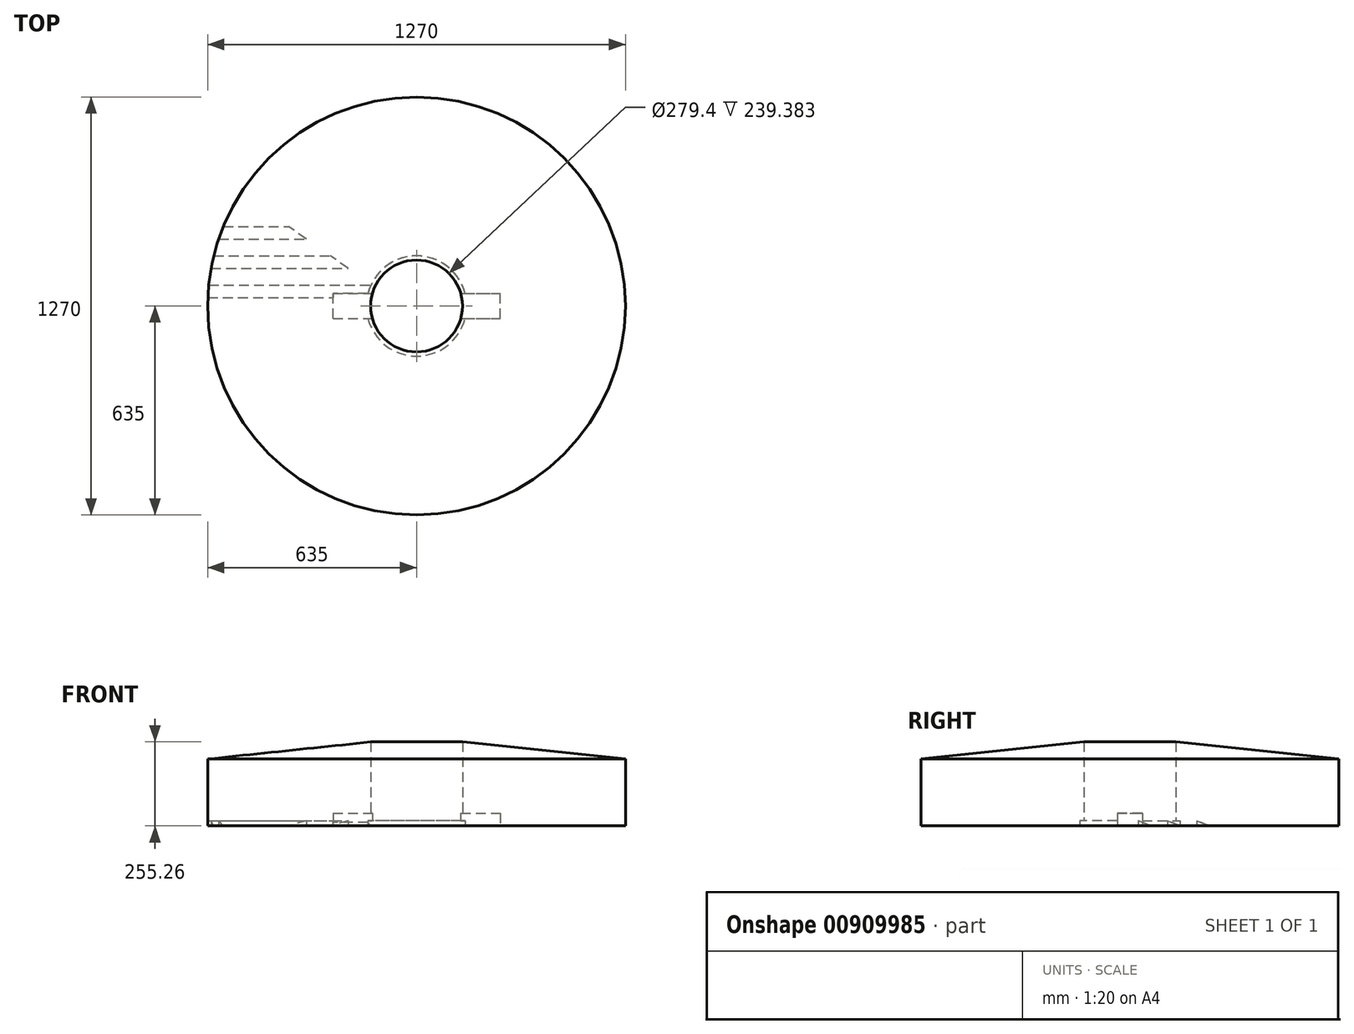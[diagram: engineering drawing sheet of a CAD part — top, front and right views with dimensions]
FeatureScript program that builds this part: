
annotation { "Feature Type Name" : "Feature", "Feature Type Description" : "" }
export const myFeature = defineFeature(function(context is Context, id is Id, definition is map)
    precondition{}
    {
        {
            var Q0;
            Q0=qCreatedBy(makeId("Front.planeOp"),FACE);
            var sketch = newSketch(context, id + "F0", { "sketchPlane" : qUnion([Q0])});
            skLineSegment(sketch, "E0", {"start": v(139.7, 0) * mm, "end": v(635, 0) * mm});
            skLineSegment(sketch, "E1", {"start": v(635, 0) * mm, "end": v(635, 203.2) * mm});
            skLineSegment(sketch, "E2", {"start": v(635, 203.2) * mm, "end": v(139.7, 255.26) * mm});
            skLineSegment(sketch, "E3", {"start": v(139.7, 255.26) * mm, "end": v(139.7, 0) * mm});
            skLineSegment(sketch, "E4", {"start": v(0, 0) * mm, "end": v(0, 255.26) * mm, "construction": true});
            skSolve(sketch);
        }
        {
            var Q0;
            Q0=makeQuery(id+"F0.imprint","IMPRINT",FACE,{"disambiguationData":[TD([[makeQuery(id+"F0.imprint","IMPRINT",EDGE,{"derivedFrom":sQuery(id+"F0.wireOp",EDGE,"E0")}),1.0]])]});
            var Q1;
            Q1=sQuery(id+"F0.wireOp",EDGE,"E4");
            revolve(context, id + "F1", {"surfaceOperationType" : NewSurfaceOperationType.NEW, "entities" : qUnion([Q0]), "axis" : qUnion([Q1]), "revolveType" : RevolveType.FULL});
        }
        {
            var Q0;
            Q0=makeQuery(id+"F1.opRevolve","SWEPT_FACE",FACE,{"disambiguationData":[OSD([sQuery(id+"F0.wireOp",EDGE,"E0")])]});
            var sketch = newSketch(context, id + "F2", { "sketchPlane" : qUnion([Q0])});
            skLineSegment(sketch, "E5.bottom", {"start": v(-634.5, -25.4) * mm, "end": v(-37.18, -25.4) * mm});
            skLineSegment(sketch, "E5.top", {"start": v(-634.5, -63.5) * mm, "end": v(-37.18, -63.5) * mm});
            skLineSegment(sketch, "E5.left", {"start": v(-634.5, -25.4) * mm, "end": v(-634.5, -63.5) * mm});
            skLineSegment(sketch, "E5.right", {"start": v(-37.18, -25.4) * mm, "end": v(-37.18, -63.5) * mm});
            skLineSegment(sketch, "E6.bottom", {"start": v(-624.63, -114.3) * mm, "end": v(-207.52, -114.3) * mm});
            skLineSegment(sketch, "E6.top", {"start": v(-624.63, -152.4) * mm, "end": v(-261.93, -152.4) * mm});
            skLineSegment(sketch, "E6.left", {"start": v(-624.63, -114.3) * mm, "end": v(-624.63, -152.4) * mm});
            skLineSegment(sketch, "E7.bottom", {"start": v(-601.61, -203.2) * mm, "end": v(-334.48, -203.2) * mm});
            skLineSegment(sketch, "E7.top", {"start": v(-601.61, -241.3) * mm, "end": v(-388.9, -241.3) * mm});
            skLineSegment(sketch, "E7.left", {"start": v(-601.61, -203.2) * mm, "end": v(-601.61, -241.3) * mm});
            skLineSegment(sketch, "E8", {"start": v(-524.9, -25.4) * mm, "end": v(-524.9, -114.3) * mm, "construction": true});
            skLineSegment(sketch, "E9", {"start": v(-524.9, -114.3) * mm, "end": v(-524.9, -203.2) * mm, "construction": true});
            skLineSegment(sketch, "E10", {"start": v(-207.52, -114.3) * mm, "end": v(-261.93, -152.4) * mm});
            skLineSegment(sketch, "E11.trimOffspring", {"start": v(-334.48, -203.2) * mm, "end": v(-388.9, -241.3) * mm});
            skCircle(sketch, "E12", {"center": v(0, 0) * mm, "radius": 152.4 * mm});
            skSolve(sketch);
        }
        {
            var Q0;
            {var subQ1=sQuery(id+"F0.wireOp",EDGE,"E0");var subQ2=makeQuery(id+"F1.opRevolve","SWEPT_EDGE",EDGE,{"disambiguationData":[OSD([subQ1,sQuery(id+"F0.wireOp",EDGE,"E1")])]});var subQ6=sQuery(id+"F2.wireOp",EDGE,"E5.top");var subQ7=makeQuery(id+"F2.imprint","INTERSECT",VERTEX,{"derivedFrom":[subQ2,subQ6]});Q0=makeQuery(id+"F2.imprint","IMPRINT",FACE,{"disambiguationData":[TD([[makeQuery(id+"F2.imprint","IMPRINT",EDGE,{"disambiguationData":[TD([[subQ7,-1.0]])],"derivedFrom":subQ6}),1.0]])]});}
            var Q1;
            {var subQ0=sQuery(id+"F2.wireOp",EDGE,"E6.bottom");Q1=makeQuery(id+"F2.imprint","IMPRINT",FACE,{"disambiguationData":[TD([[makeQuery(id+"F2.imprint","IMPRINT",EDGE,{"derivedFrom":subQ0}),-1.0]])]});}
            var Q2;
            {var subQ0=sQuery(id+"F2.wireOp",EDGE,"E7.bottom");Q2=makeQuery(id+"F2.imprint","IMPRINT",FACE,{"disambiguationData":[TD([[makeQuery(id+"F2.imprint","IMPRINT",EDGE,{"derivedFrom":subQ0}),-1.0]])]});}
            extrude(context, id + "F3", {"entities" : qUnion([Q0, Q1, Q2]), "operationType" : NewBodyOperationType.REMOVE, "oppositeDirection" : true, "depth" : 15.88 * mm, "offsetDistance" : 25 * mm});
        }
        {
            var Q0;
            {var subQ0=sQuery(id+"F2.wireOp",EDGE,"E12");var subQ1=sQuery(id+"F2.wireOp",EDGE,"E5.bottom");var subQ2=makeQuery(id+"F2.imprint","INTERSECT",VERTEX,{"derivedFrom":[subQ1,subQ0]});Q0=makeQuery(id+"F2.imprint","IMPRINT",FACE,{"disambiguationData":[TD([[makeQuery(id+"F2.imprint","IMPRINT",EDGE,{"disambiguationData":[TD([[subQ2,1.0]])],"derivedFrom":subQ0}),1.0]])]});}
            var Q1;
            {var subQ0=sQuery(id+"F2.wireOp",EDGE,"E5.right");Q1=makeQuery(id+"F2.imprint","IMPRINT",FACE,{"disambiguationData":[TD([[makeQuery(id+"F2.imprint","IMPRINT",EDGE,{"derivedFrom":subQ0}),-1.0]])]});}
            var Q2;
            {var subQ0=sQuery(id+"F2.wireOp",EDGE,"E12");var subQ1=sQuery(id+"F2.wireOp",EDGE,"E5.bottom");var subQ2=makeQuery(id+"F2.imprint","INTERSECT",VERTEX,{"derivedFrom":[subQ1,subQ0]});Q2=makeQuery(id+"F2.imprint","IMPRINT",FACE,{"disambiguationData":[TD([[makeQuery(id+"F2.imprint","IMPRINT",EDGE,{"disambiguationData":[TD([[subQ2,-1.0]])],"derivedFrom":subQ0}),1.0]])]});}
            extrude(context, id + "F4", {"entities" : qUnion([Q0, Q1, Q2]), "operationType" : NewBodyOperationType.REMOVE, "oppositeDirection" : true, "depth" : 15.88 * mm, "offsetDistance" : 25 * mm});
        }
        {
            var Q0;
            Q0=makeQuery(id+"F3.boolean.opBoolean","COPY",EDGE,{"derivedFrom":makeQuery(id+"F3.opExtrude","CAP_EDGE",EDGE,{"disambiguationData":[OSD([sQuery(id+"F2.wireOp",EDGE,"E5.top")])],"isStart":false})});
            var Q1;
            Q1=makeQuery(id+"F3.boolean.opBoolean","COPY",EDGE,{"derivedFrom":makeQuery(id+"F3.opExtrude","CAP_EDGE",EDGE,{"disambiguationData":[OSD([sQuery(id+"F2.wireOp",EDGE,"E6.top")])],"isStart":false})});
            var Q2;
            Q2=makeQuery(id+"F3.boolean.opBoolean","COPY",EDGE,{"derivedFrom":makeQuery(id+"F3.opExtrude","CAP_EDGE",EDGE,{"disambiguationData":[OSD([sQuery(id+"F2.wireOp",EDGE,"E7.top")])],"isStart":false})});
            chamfer(context, id + "F5", {"entities" : qUnion([Q0, Q1, Q2]), "chamferType" : ChamferType.TWO_OFFSETS, "width1" : 38.1 * mm, "oppositeDirection" : false, "width2" : 15.88 * mm, "tangentPropagation" : true});
        }
        {
            var Q0;
            {var subQ13=sQuery(id+"F2.wireOp",EDGE,"E6.bottom");Q0=makeQuery(id+"F2.imprint","IMPRINT",FACE,{"disambiguationData":[TD([[makeQuery(id+"F2.imprint","IMPRINT",EDGE,{"derivedFrom":subQ13}),1.0]])]});}
            var sketch = newSketch(context, id + "F6", { "sketchPlane" : qUnion([Q0])});
            skLineSegment(sketch, "E13.bottom", {"start": v(-254, 38.1) * mm, "end": v(254, 38.1) * mm});
            skLineSegment(sketch, "E13.top", {"start": v(-254, -38.1) * mm, "end": v(254, -38.1) * mm});
            skLineSegment(sketch, "E13.left", {"start": v(-254, 38.1) * mm, "end": v(-254, -38.1) * mm});
            skLineSegment(sketch, "E13.right", {"start": v(254, 38.1) * mm, "end": v(254, -38.1) * mm});
            skLineSegment(sketch, "E14", {"start": v(-254, 0) * mm, "end": v(254, 0) * mm, "construction": true});
            skLineSegment(sketch, "E15", {"start": v(0, 38.1) * mm, "end": v(0, -38.1) * mm, "construction": true});
            skSolve(sketch);
        }
        {
            var Q0;
            {var subQ0=sQuery(id+"F6.wireOp",EDGE,"E13.bottom");var subQ1=sQuery(id+"F2.wireOp",EDGE,"E12");var subQ2=makeQuery(id+"F2.imprint","IMPRINT",EDGE,{"disambiguationData":[TD([[makeQuery(id+"F2.imprint","INTERSECT",VERTEX,{"derivedFrom":[sQuery(id+"F2.wireOp",EDGE,"E5.bottom"),subQ1]}),1.0]])],"derivedFrom":subQ1});var subQ3=makeQuery(id+"F6.imprint","INTERSECT",VERTEX,{"disambiguationData":[OD(0.0)],"derivedFrom":[subQ2,subQ0]});Q0=makeQuery(id+"F6.imprint","IMPRINT",FACE,{"disambiguationData":[TD([[makeQuery(id+"F6.imprint","IMPRINT",EDGE,{"disambiguationData":[TD([[subQ3,-1.0]])],"derivedFrom":subQ0}),-1.0]])]});}
            var Q1;
            {var subQ0=sQuery(id+"F6.wireOp",EDGE,"E13.left");Q1=makeQuery(id+"F6.imprint","IMPRINT",FACE,{"disambiguationData":[TD([[makeQuery(id+"F6.imprint","IMPRINT",EDGE,{"derivedFrom":subQ0}),1.0]])]});}
            var Q2;
            {var subQ0=sQuery(id+"F6.wireOp",EDGE,"E13.right");Q2=makeQuery(id+"F6.imprint","IMPRINT",FACE,{"disambiguationData":[TD([[makeQuery(id+"F6.imprint","IMPRINT",EDGE,{"derivedFrom":subQ0}),-1.0]])]});}
            extrude(context, id + "F7", {"entities" : qUnion([Q0, Q1, Q2]), "operationType" : NewBodyOperationType.REMOVE, "oppositeDirection" : true, "depth" : 38.1 * mm, "offsetDistance" : 25 * mm});
        }
    });
